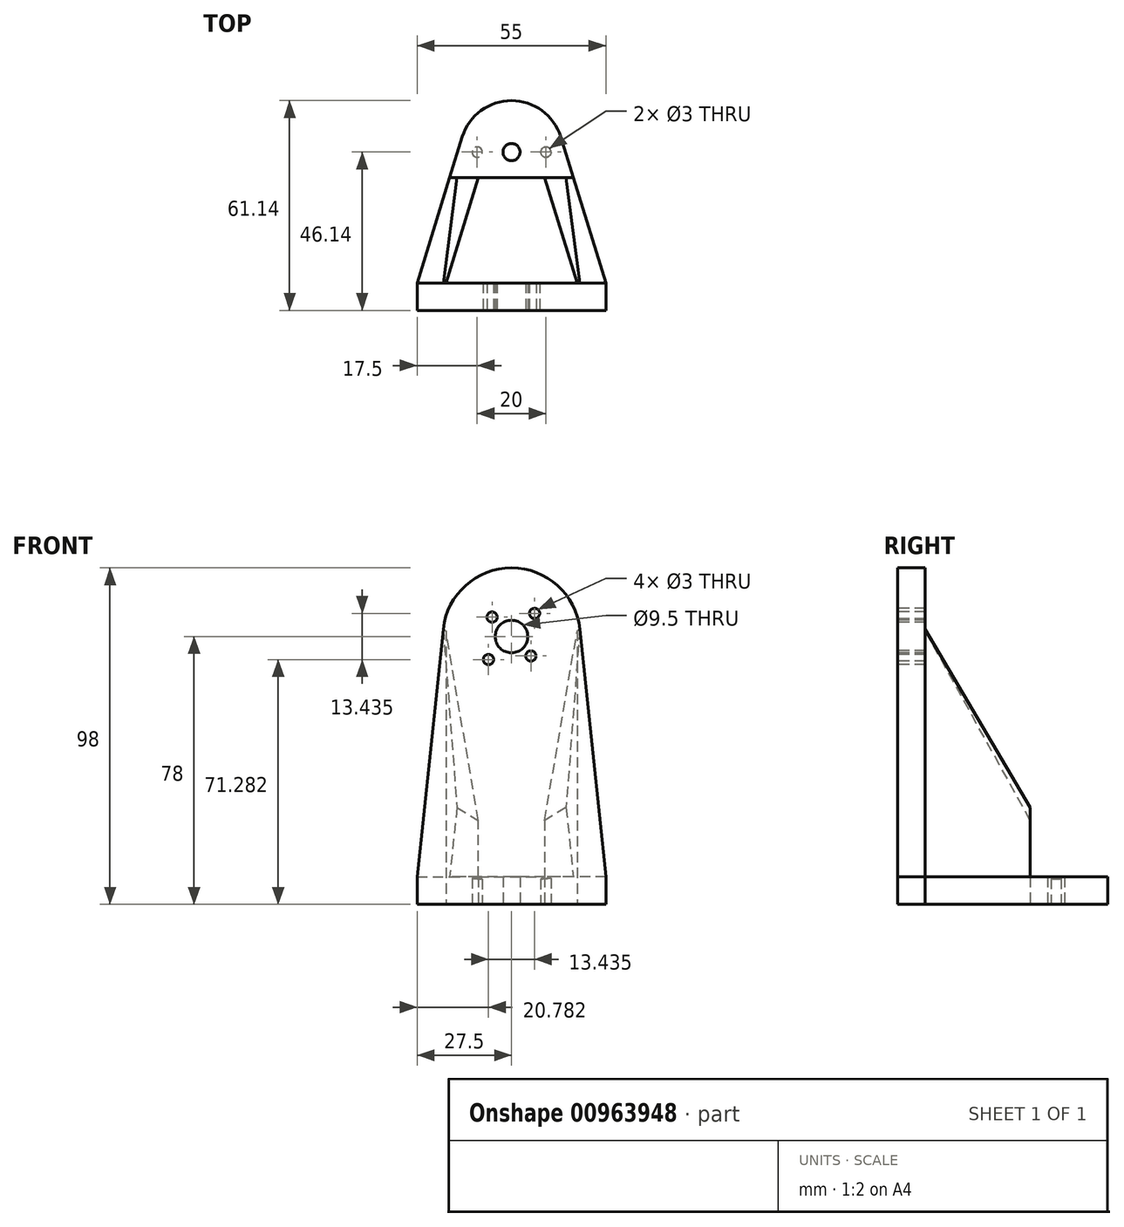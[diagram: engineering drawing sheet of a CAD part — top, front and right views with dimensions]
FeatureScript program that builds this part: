
annotation { "Feature Type Name" : "Feature", "Feature Type Description" : "" }
export const myFeature = defineFeature(function(context is Context, id is Id, definition is map)
    precondition{}
    {
        {
            var Q0;
            Q0=qCreatedBy(makeId("Top.planeOp"),FACE);
            var sketch = newSketch(context, id + "F0", { "sketchPlane" : qUnion([Q0])});
            skLineSegment(sketch, "E0.bottom", {"start": v(-27.5, 0) * mm, "end": v(27.5, 0) * mm});
            skLineSegment(sketch, "E0.top", {"start": v(-27.5, 8) * mm, "end": v(27.5, 8) * mm});
            skLineSegment(sketch, "E0.left", {"start": v(-27.5, 0) * mm, "end": v(-27.5, 8) * mm});
            skLineSegment(sketch, "E0.right", {"start": v(27.5, 0) * mm, "end": v(27.5, 8) * mm});
            skLineSegment(sketch, "E1", {"start": v(0, 8) * mm, "end": v(0, 46.14) * mm, "construction": true});
            skArc(sketch, "E2", {"start": v(14.33, 50.57) * mm, "mid": v(0, 61.14) * mm, "end": v(-14.33, 50.57) * mm});
            skLineSegment(sketch, "E3", {"start": v(-27.5, 8) * mm, "end": v(-16.47, 43.64) * mm});
            skLineSegment(sketch, "E4", {"start": v(27.5, 8) * mm, "end": v(16.47, 43.64) * mm});
            skCircle(sketch, "E5", {"center": v(0, 46.14) * mm, "radius": 2.5 * mm});
            skLineSegment(sketch, "E6", {"start": v(-10, 46.14) * mm, "end": v(10, 46.14) * mm, "construction": true});
            skCircle(sketch, "E7", {"center": v(-10, 46.14) * mm, "radius": 1.5 * mm});
            skCircle(sketch, "E8", {"center": v(10, 46.14) * mm, "radius": 1.5 * mm});
            skLineSegment(sketch, "E9", {"start": v(-16.47, 43.64) * mm, "end": v(-8.1, 43.64) * mm, "construction": true});
            skLineSegment(sketch, "E10", {"start": v(0, 43.64) * mm, "end": v(0, 38.64) * mm, "construction": true});
            skLineSegment(sketch, "E11", {"start": v(-16.47, 43.64) * mm, "end": v(-14.33, 50.57) * mm});
            skLineSegment(sketch, "E12", {"start": v(16.47, 43.64) * mm, "end": v(14.33, 50.57) * mm});
            skLineSegment(sketch, "E13", {"start": v(-19.13, 8) * mm, "end": v(-9.65, 38.64) * mm});
            skLineSegment(sketch, "E14", {"start": v(9.65, 38.64) * mm, "end": v(19.13, 8) * mm});
            skLineSegment(sketch, "E15", {"start": v(-9.65, 38.64) * mm, "end": v(9.65, 38.64) * mm});
            skLineSegment(sketch, "E16.trimOffspring", {"start": v(-8.1, 43.64) * mm, "end": v(16.47, 43.64) * mm, "construction": true});
            skSolve(sketch);
        }
        {
            var Q0;
            Q0 = qSketchRegion(id + "F0", true);
            extrude(context, id + "F1", {"entities" : qUnion([Q0]), "depth" : 8 * mm, "offsetDistance" : 25 * mm});
        }
        {
            var Q0;
            Q0=makeQuery(id+"F1.opExtrude","SWEPT_FACE",FACE,{"disambiguationData":[OSD([sQuery(id+"F0.wireOp",EDGE,"E0.bottom")])]});
            var sketch = newSketch(context, id + "F2", { "sketchPlane" : qUnion([Q0])});
            skLineSegment(sketch, "E17", {"start": v(0, 0) * mm, "end": v(0, 78) * mm, "construction": true});
            skArc(sketch, "E18", {"start": v(19.89, 80.1) * mm, "mid": v(0, 98) * mm, "end": v(-19.89, 80.1) * mm});
            skLineSegment(sketch, "E19", {"start": v(-27.5, 8) * mm, "end": v(-19.89, 80.1) * mm});
            skLineSegment(sketch, "E20", {"start": v(27.5, 8) * mm, "end": v(19.89, 80.1) * mm});
            skSolve(sketch);
        }
        {
            var Q0;
            Q0 = qSketchRegion(id + "F2", true);
            var Q1;
            Q1=makeQuery(id+"F2.imprint","IMPRINT",FACE,{"disambiguationData":[TD([[makeQuery(id+"F2.imprint","IMPRINT",EDGE,{"derivedFrom":sQuery(id+"F2.wireOp",EDGE,"E18")}),1.0]])]});
            var Q2;
            {var subQ0=sQuery(id+"F0.wireOp",EDGE,"E0.bottom");Q2=makeQuery(id+"F2.imprint","IMPRINT",FACE,{"disambiguationData":[TD([[makeQuery(id+"F2.imprint","IMPRINT",EDGE,{"derivedFrom":makeQuery(id+"F1.opExtrude","CAP_EDGE",EDGE,{"disambiguationData":[OSD([subQ0])],"isStart":true})}),1.0]])]});}
            extrude(context, id + "F3", {"entities" : qUnion([Q0, Q1, Q2]), "operationType" : NewBodyOperationType.ADD, "oppositeDirection" : true, "depth" : 8 * mm, "offsetDistance" : 25 * mm});
        }
        {
            var Q0;
            {var subQ0=sQuery(id+"F0.wireOp",EDGE,"E0.bottom");Q0=makeQuery(id+"F3.boolean.opBoolean","MERGE",FACE,{"derivedFrom":[makeQuery(id+"F1.opExtrude","SWEPT_FACE",FACE,{"disambiguationData":[OSD([subQ0])]}),makeQuery(id+"F3.opExtrude","CAP_FACE",FACE,{"disambiguationData":[OSD([subQ0,sQuery(id+"F0.wireOp",EDGE,"E0.left"),sQuery(id+"F0.wireOp",EDGE,"E0.right"),sQuery(id+"F2.wireOp",EDGE,"E18"),sQuery(id+"F2.wireOp",EDGE,"E19"),sQuery(id+"F2.wireOp",EDGE,"E20")])],"isStart":true})]});}
            var sketch = newSketch(context, id + "F4", { "sketchPlane" : qUnion([Q0])});
            skPoint(sketch, "E21.0", {"position": v(0, 78) * mm});
            skCircle(sketch, "E22", {"center": v(0, 78) * mm, "radius": 4.75 * mm});
            skLineSegment(sketch, "E23", {"start": v(-6.72, 71.28) * mm, "end": v(6.72, 84.72) * mm, "construction": true});
            skLineSegment(sketch, "E24", {"start": v(5.66, 72.34) * mm, "end": v(-5.66, 83.66) * mm, "construction": true});
            skLineSegment(sketch, "E25", {"start": v(-20.11, 78) * mm, "end": v(20.11, 78) * mm, "construction": true});
            skCircle(sketch, "E26", {"center": v(-5.66, 83.66) * mm, "radius": 1.5 * mm});
            skCircle(sketch, "E27", {"center": v(6.72, 84.72) * mm, "radius": 1.5 * mm});
            skCircle(sketch, "E28", {"center": v(5.66, 72.34) * mm, "radius": 1.5 * mm});
            skCircle(sketch, "E29", {"center": v(-6.72, 71.28) * mm, "radius": 1.5 * mm});
            skSolve(sketch);
        }
        {
            var Q0;
            Q0 = qSketchRegion(id + "F4", true);
            var Q1;
            Q1=makeQuery(id+"F3.boolean.opBoolean","MERGE",FACE,{"derivedFrom":[makeQuery(id+"F1.opExtrude","SWEPT_FACE",FACE,{"disambiguationData":[OSD([sQuery(id+"F0.wireOp",EDGE,"E0.top")])]}),makeQuery(id+"F3.opExtrude","CAP_FACE",FACE,{"disambiguationData":[OSD([sQuery(id+"F0.wireOp",EDGE,"E0.bottom"),sQuery(id+"F0.wireOp",EDGE,"E0.left"),sQuery(id+"F0.wireOp",EDGE,"E0.right"),sQuery(id+"F2.wireOp",EDGE,"E18"),sQuery(id+"F2.wireOp",EDGE,"E19"),sQuery(id+"F2.wireOp",EDGE,"E20")])],"isStart":false})]});
            extrude(context, id + "F5", {"entities" : qUnion([Q0]), "operationType" : NewBodyOperationType.REMOVE, "endBound" : BoundingType.UP_TO_SURFACE, "oppositeDirection" : true, "depth" : 25 * mm, "endBoundEntityFace" : qUnion([Q1]), "offsetDistance" : 25 * mm});
        }
        {
            var Q0;
            Q0=makeQuery(id+"F1.opExtrude","CAP_VERTEX",VERTEX,{"disambiguationData":[OSD([sQuery(id+"F0.wireOp",EDGE,"E2"),sQuery(id+"F0.wireOp",EDGE,"E12")])],"isStart":false});
            var Q1;
            {var subQ0=sQuery(id+"F0.wireOp",EDGE,"E0.right");Q1=makeQuery(id+"F3.boolean.opBoolean","MERGE",VERTEX,{"derivedFrom":[makeQuery(id+"F1.opExtrude","CAP_VERTEX",VERTEX,{"disambiguationData":[OSD([sQuery(id+"F0.wireOp",EDGE,"E0.top"),subQ0,sQuery(id+"F0.wireOp",EDGE,"E4")])],"isStart":false}),makeQuery(id+"F3.opExtrude","CAP_VERTEX",VERTEX,{"disambiguationData":[OSD([sQuery(id+"F0.wireOp",EDGE,"E0.bottom"),subQ0,sQuery(id+"F2.wireOp",EDGE,"E20")])],"isStart":false})]});}
            var Q2;
            Q2=makeQuery(id+"F3.opExtrude","CAP_VERTEX",VERTEX,{"disambiguationData":[OSD([sQuery(id+"F2.wireOp",EDGE,"E18"),sQuery(id+"F2.wireOp",EDGE,"E20")])],"isStart":false});
            cPlane(context, id + "F6", {"entities" : qUnion([Q0, Q1, Q2]), "cplaneType" : CPlaneType.THREE_POINT, "offset" : 25 * mm, "width" : 150 * mm, "height" : 150 * mm});
        }
        {
            var Q0;
            Q0=qCreatedBy(id+"F6.planeOp",FACE);
            var sketch = newSketch(context, id + "F7", { "sketchPlane" : qUnion([Q0])});
            skLineSegment(sketch, "E30.0", {"start": v(-0.64, 5.07) * mm, "end": v(-0.64, 77.57) * mm});
            skLineSegment(sketch, "E31.0", {"start": v(-0.64, 5.07) * mm, "end": v(43.9, 6.45) * mm});
            skLineSegment(sketch, "E32", {"start": v(-0.64, 77.57) * mm, "end": v(43.9, 6.45) * mm});
            skSolve(sketch);
        }
        {
            var Q0;
            Q0 = qSketchRegion(id + "F7", true);
            var Q1;
            Q1=makeQuery(id+"F1.opExtrude","SWEPT_FACE",FACE,{"disambiguationData":[OSD([sQuery(id+"F0.wireOp",EDGE,"E14")])]});
            extrude(context, id + "F8", {"entities" : qUnion([Q0]), "operationType" : NewBodyOperationType.ADD, "endBound" : BoundingType.UP_TO_SURFACE, "oppositeDirection" : true, "depth" : 25 * mm, "endBoundEntityFace" : qUnion([Q1]), "offsetDistance" : 25 * mm});
        }
        {
            var Q0;
            Q0=makeQuery(id+"F1.opExtrude","CAP_VERTEX",VERTEX,{"disambiguationData":[OSD([sQuery(id+"F0.wireOp",EDGE,"E2"),sQuery(id+"F0.wireOp",EDGE,"E11")])],"isStart":false});
            var Q1;
            {var subQ0=sQuery(id+"F0.wireOp",EDGE,"E0.left");Q1=makeQuery(id+"F3.boolean.opBoolean","MERGE",VERTEX,{"derivedFrom":[makeQuery(id+"F1.opExtrude","CAP_VERTEX",VERTEX,{"disambiguationData":[OSD([sQuery(id+"F0.wireOp",EDGE,"E0.top"),subQ0,sQuery(id+"F0.wireOp",EDGE,"E3")])],"isStart":false}),makeQuery(id+"F3.opExtrude","CAP_VERTEX",VERTEX,{"disambiguationData":[OSD([sQuery(id+"F0.wireOp",EDGE,"E0.bottom"),subQ0,sQuery(id+"F2.wireOp",EDGE,"E19")])],"isStart":false})]});}
            var Q2;
            Q2=makeQuery(id+"F3.opExtrude","CAP_VERTEX",VERTEX,{"disambiguationData":[OSD([sQuery(id+"F2.wireOp",EDGE,"E18"),sQuery(id+"F2.wireOp",EDGE,"E19")])],"isStart":false});
            cPlane(context, id + "F9", {"entities" : qUnion([Q0, Q1, Q2]), "cplaneType" : CPlaneType.THREE_POINT, "offset" : 25 * mm, "width" : 150 * mm, "height" : 150 * mm});
        }
        {
            var Q0;
            Q0=qCreatedBy(id+"F9.planeOp",FACE);
            var sketch = newSketch(context, id + "F10", { "sketchPlane" : qUnion([Q0])});
            skLineSegment(sketch, "E33.0", {"start": v(-0.64, 5.07) * mm, "end": v(-0.64, 77.57) * mm});
            skLineSegment(sketch, "E34.0", {"start": v(-0.64, 5.07) * mm, "end": v(43.9, 6.45) * mm});
            skLineSegment(sketch, "E35", {"start": v(-0.64, 77.57) * mm, "end": v(43.9, 6.45) * mm});
            skSolve(sketch);
        }
        {
            var Q0;
            Q0 = qSketchRegion(id + "F10", true);
            var Q1;
            Q1=makeQuery(id+"F1.opExtrude","SWEPT_FACE",FACE,{"disambiguationData":[OSD([sQuery(id+"F0.wireOp",EDGE,"E13")])]});
            extrude(context, id + "F11", {"entities" : qUnion([Q0]), "operationType" : NewBodyOperationType.ADD, "endBound" : BoundingType.UP_TO_SURFACE, "depth" : 25 * mm, "endBoundEntityFace" : qUnion([Q1]), "offsetDistance" : 25 * mm});
        }
        {
            var Q0;
            Q0=makeQuery(id+"F1.opExtrude","CAP_FACE",FACE,{"disambiguationData":[OSD([sQuery(id+"F0.wireOp",EDGE,"E0.bottom"),sQuery(id+"F0.wireOp",EDGE,"E0.top"),sQuery(id+"F0.wireOp",EDGE,"E0.left"),sQuery(id+"F0.wireOp",EDGE,"E0.right"),sQuery(id+"F0.wireOp",EDGE,"E2"),sQuery(id+"F0.wireOp",EDGE,"E3"),sQuery(id+"F0.wireOp",EDGE,"E4"),sQuery(id+"F0.wireOp",EDGE,"E5"),sQuery(id+"F0.wireOp",EDGE,"E7"),sQuery(id+"F0.wireOp",EDGE,"E8"),sQuery(id+"F0.wireOp",EDGE,"E11"),sQuery(id+"F0.wireOp",EDGE,"E12"),sQuery(id+"F0.wireOp",EDGE,"E13"),sQuery(id+"F0.wireOp",EDGE,"E14"),sQuery(id+"F0.wireOp",EDGE,"E15")])],"isStart":false});
            var sketch = newSketch(context, id + "F12", { "sketchPlane" : qUnion([Q0])});
            skLineSegment(sketch, "E36.0.2", {"start": v(-9.65, 38.64) * mm, "end": v(9.65, 38.64) * mm});
            skArc(sketch, "E36.0.5", {"start": v(14.33, 50.57) * mm, "mid": v(0, 61.14) * mm, "end": v(-14.33, 50.57) * mm});
            skLineSegment(sketch, "E37.0", {"start": v(-18.02, 38.64) * mm, "end": v(-14.33, 50.57) * mm});
            skLineSegment(sketch, "E38.0", {"start": v(18.02, 38.64) * mm, "end": v(14.33, 50.57) * mm});
            skLineSegment(sketch, "E39", {"start": v(9.65, 38.64) * mm, "end": v(18.02, 38.64) * mm});
            skLineSegment(sketch, "E40", {"start": v(-9.65, 38.64) * mm, "end": v(-18.02, 38.64) * mm});
            skPoint(sketch, "E41.orphan", {"position": v(-27.5, 8) * mm});
            skPoint(sketch, "E42.orphan", {"position": v(27.5, 8) * mm});
            skPoint(sketch, "E36.0.3.end.orphan", {"position": v(6.83, 47.76) * mm});
            skPoint(sketch, "E36.0.0.end.orphan", {"position": v(-6.83, 47.76) * mm});
            skSolve(sketch);
        }
        {
            var Q0;
            Q0 = qSketchRegion(id + "F12", true);
            extrude(context, id + "F13", {"entities" : qUnion([Q0]), "operationType" : NewBodyOperationType.REMOVE, "depth" : 25 * mm, "offsetDistance" : 25 * mm});
        }
    });
